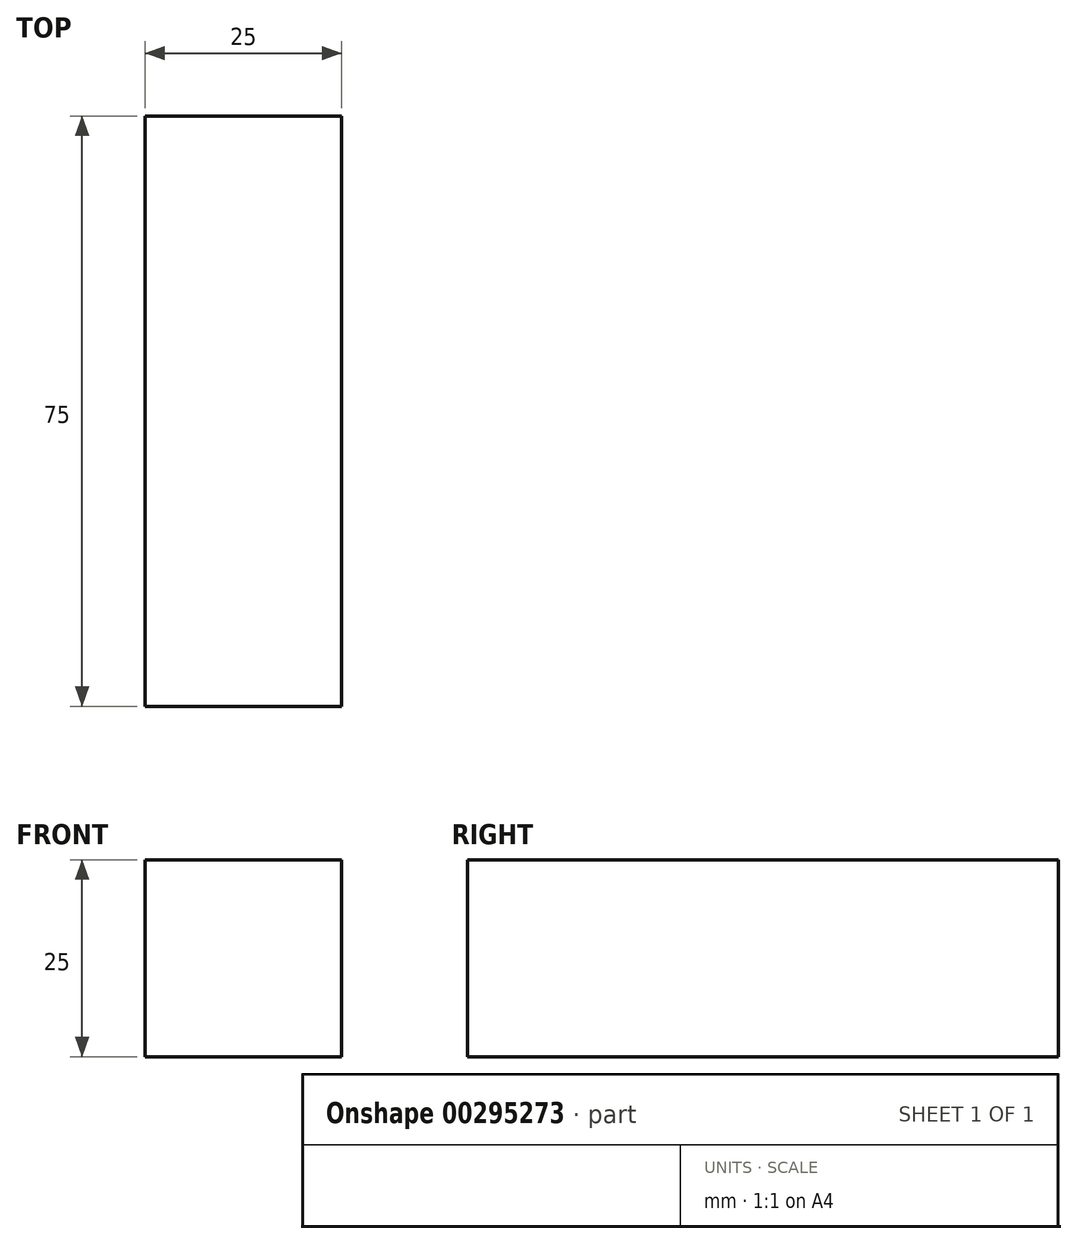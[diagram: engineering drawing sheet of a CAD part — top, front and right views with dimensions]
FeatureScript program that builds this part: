
annotation { "Feature Type Name" : "Feature", "Feature Type Description" : "" }
export const myFeature = defineFeature(function(context is Context, id is Id, definition is map)
    precondition{}
    {
        {
            var Q0;
            Q0=qCreatedBy(makeId("Right.planeOp"),FACE);
            var sketch = newSketch(context, id + "F0", { "sketchPlane" : qUnion([Q0])});
            skLineSegment(sketch, "E0.bottom", {"start": v(0, 0) * mm, "end": v(75, 0) * mm});
            skLineSegment(sketch, "E0.top", {"start": v(0, 25) * mm, "end": v(75, 25) * mm});
            skLineSegment(sketch, "E0.left", {"start": v(0, 0) * mm, "end": v(0, 25) * mm});
            skLineSegment(sketch, "E0.right", {"start": v(75, 0) * mm, "end": v(75, 25) * mm});
            skSolve(sketch);
        }
        {
            var Q0;
            Q0=makeQuery(id+"F0.imprint","IMPRINT",FACE,{"disambiguationData":[TD([[makeQuery(id+"F0.imprint","IMPRINT",EDGE,{"derivedFrom":sQuery(id+"F0.wireOp",EDGE,"E0.bottom")}),1.0]])]});
            extrude(context, id + "F1", {"entities" : qUnion([Q0]), "depth" : 25 * mm});
        }
    });
